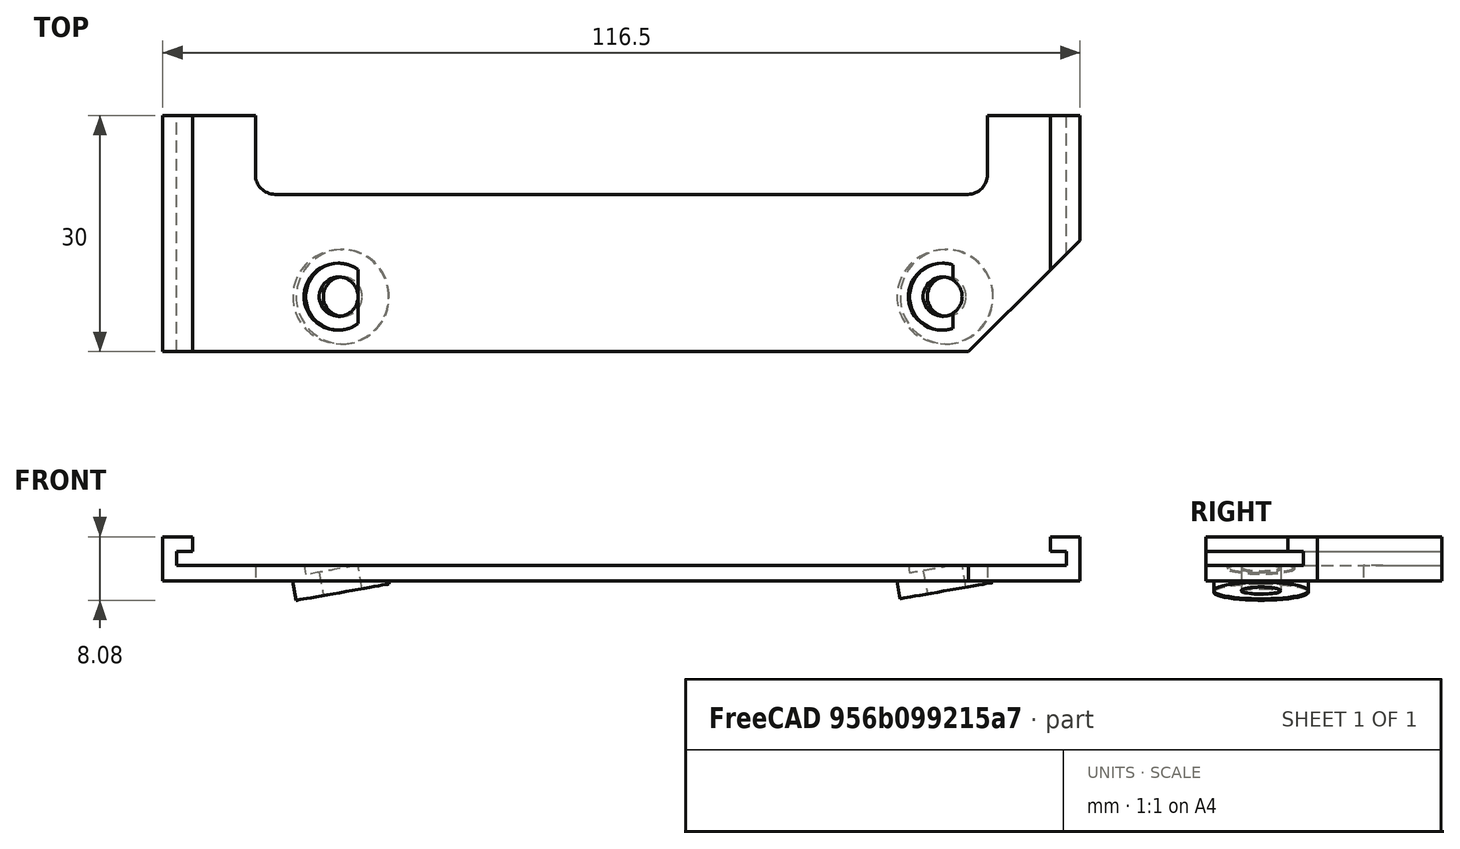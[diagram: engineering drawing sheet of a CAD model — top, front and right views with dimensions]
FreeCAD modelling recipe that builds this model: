
FCSTD DOCUMENT  (FreeCAD 0.21R33668 +7 (Git))
Label: DecentXL-Left-Bracket
License: All rights reserved
LicenseURL: http://en.wikipedia.org/wiki/All_rights_reserved
objects: Sketcher::SketchObject×9, PartDesign::Pocket×7, PartDesign::Line×2, PartDesign::Pad×2, Part::Box×1, PartDesign::FeatureBase×1, PartDesign::Body×1, Mesh::Feature×1
note: 32 computed .brp shape members not serialized (recipe doc carries the construction recipe); baked Part::Feature solids carry a one-line shape summary decoded from their .brp

FEATURE [Part::Box] Box  label="Cube"
  AttacherType = Attacher::AttachEngine3D
  Height = 5.6
  Length = 116.5
  Width = 30
FEATURE [PartDesign::FeatureBase] BaseFeature
  BaseFeature = -> Box
FEATURE [Sketcher::SketchObject] Sketch
  ExternalGeometry = -> [BaseFeature]
  FullyConstrained = true
  MapMode = 5
  Placement = pos=(0,0,0) rot=(1,0,0;1.5708rad)
  Support = -> [BaseFeature]
  sketch-geometry (10):
    g0: LineSegment StartX=3.75 StartY=5.6 StartZ=0 EndX=3.75 EndY=3.75 EndZ=0
    g1: LineSegment StartX=3.75 StartY=3.75 StartZ=0 EndX=1.75 EndY=3.75 EndZ=0
    g2: LineSegment StartX=1.75 StartY=3.75 StartZ=0 EndX=1.75 EndY=1.95 EndZ=0
    g3: LineSegment StartX=1.75 StartY=1.95 StartZ=0 EndX=114.75 EndY=1.95 EndZ=0
    g4: LineSegment StartX=114.75 StartY=1.95 StartZ=0 EndX=114.75 EndY=3.75 EndZ=0
    g5: LineSegment StartX=114.75 StartY=3.75 StartZ=0 EndX=112.75 EndY=3.75 EndZ=0
    g6: LineSegment StartX=112.75 StartY=3.75 StartZ=0 EndX=112.75 EndY=5.6 EndZ=0
    g7: LineSegment StartX=112.75 StartY=5.6 StartZ=0 EndX=3.75 EndY=5.6 EndZ=0
    g8: LineSegment StartX=0 StartY=5.6 StartZ=0 EndX=3.75 EndY=5.6 EndZ=0
    g9: LineSegment StartX=112.75 StartY=5.6 StartZ=0 EndX=116.5 EndY=5.6 EndZ=0
  constraints (28):
    c: PointOnObject(g0,g-3)
    c: Vertical(g0)
    c: Coincident(g0,g1)
    c: Horizontal(g1)
    c: Coincident(g1,g2)
    c: Vertical(g2)
    c: Coincident(g2,g3)
    c: Horizontal(g3)
    c: Coincident(g3,g4)
    c: Vertical(g4)
    c: Coincident(g4,g5)
    c: Horizontal(g5)
    c: Coincident(g5,g6)
    c: PointOnObject(g6,g-3)
    c: Vertical(g6)
    c: Coincident(g6,g7)
    c: Coincident(g7,g0)
    c: Equal(g2,g4)
    c: DistanceY(g4,g4) = 1.8
    c: DistanceX(g3,g3) = 113
    c: Equal(g1,g5)
    c: Coincident(g8,g-3)
    c: Coincident(g8,g0)
    c: Coincident(g9,g6)
    c: Coincident(g9,g-3)
    c: Equal(g8,g9)
    c: DistanceY(g6,g6) = 1.85
    c: DistanceX(g1,g1) = 2
FEATURE [PartDesign::Pocket] Pocket
  BaseFeature = -> BaseFeature
  Direction = (0,1,-2e-16)
  Length = 0
  Length2 = 5
  Profile = -> Sketch
  ReferenceAxis = -> Sketch [N_Axis]
  Type = 3
  UpToFace = -> BaseFeature [Face4]
FEATURE [Sketcher::SketchObject] Sketch001
  ExternalGeometry = -> [Pocket]
  FullyConstrained = true
  MapMode = 5
  Placement = pos=(0,0,0) rot=(1,0,0;3.14159rad)
  Support = -> [Pocket]
  sketch-geometry (3):
    g0: LineSegment StartX=102.358 StartY=-1.8e-15 StartZ=0 EndX=116.5 EndY=1e-16 EndZ=0
    g1: LineSegment StartX=116.5 StartY=1e-16 StartZ=0 EndX=116.5 EndY=-14.1421 EndZ=0
    g2: LineSegment StartX=116.5 StartY=-14.1421 StartZ=0 EndX=102.358 EndY=-1.8e-15 EndZ=0
  constraints (8):
    c: PointOnObject(g0,g-4)
    c: Coincident(g0,g-4)
    c: Coincident(g0,g1)
    c: PointOnObject(g1,g-3)
    c: Coincident(g1,g2)
    c: Coincident(g2,g0)
    c: Equal(g1,g0)
    c: Distance(g2) = 20
FEATURE [PartDesign::Pocket] Pocket001
  BaseFeature = -> Pocket
  Direction = (0,0,1)
  Length = 0
  Length2 = 5
  Profile = -> Sketch001
  ReferenceAxis = -> Sketch001 [N_Axis]
  Type = 3
  UpToFace = -> Pocket [Face7]
FEATURE [PartDesign::Line] DatumLine
  AttacherType = Attacher::AttachEngineLine
  AttachmentOffset = pos=(-20.5,0,0) rot=(0,0,1;0rad)
  Length = 20
  MapMode = 29
  Placement = pos=(22.25,4e-16,1.95) rot=(0,0.707107,0.707107;3.14159rad)
  ResizeMode = 0
  Support = -> [Pocket001]
FEATURE [Sketcher::SketchObject] Sketch002
  AttachmentOffset = pos=(0.607769,0,-7.3105) rot=(0,-1,0;0.174533rad)
  ExternalGeometry = -> [DatumLine]
  FullyConstrained = true
  MapMode = 5
  Placement = pos=(0.607769,-1.2e-15,-5.3605) rot=(0,-1,0;0.174533rad)
  Support = -> [Pocket001]
  expr: .AttachmentOffset.Base.x = 3.5 mm * sin(10)
  expr: .AttachmentOffset.Base.z = -sin(10) * DatumLine.Placement.Base.x - 3.5 mm * cos(10)
  sketch-geometry (1):
    g0: Circle CenterX=22.5829 CenterY=7 CenterZ=0 NormalX=0 NormalY=0 NormalZ=1 AngleXU=0 Radius=2.5
  constraints (3):
    c: PointOnObject(g0,g-3)
    c: Diameter(g0) = 5
    c: DistanceY(g-1,g0) = 7
FEATURE [Sketcher::SketchObject] Sketch003
  AttachmentOffset = pos=(0.607769,0,-7.3105) rot=(0,-1,0;0.174533rad)
  ExternalGeometry = -> [DatumLine]
  FullyConstrained = true
  MapMode = 5
  Placement = pos=(0.607769,-1.2e-15,-5.3605) rot=(0,-1,0;0.174533rad)
  Support = -> [Pocket001]
  expr: .AttachmentOffset.Base.x = 3.5 * sin(10)
  expr: .AttachmentOffset.Base.z = -sin(10) * DatumLine.Placement.Base.x - 3.5 mm * cos(10)
  sketch-geometry (1):
    g0: Circle CenterX=22.5829 CenterY=7 CenterZ=0 NormalX=0 NormalY=0 NormalZ=1 AngleXU=0 Radius=6
  constraints (3):
    c: Diameter(g0) = 12
    c: DistanceY(g-1,g0) = 7
    c: PointOnObject(g0,g-3)
FEATURE [PartDesign::Line] DatumLine001
  AttacherType = Attacher::AttachEngineLine
  AttachmentOffset = pos=(15.75,0,0) rot=(0,0,1;0rad)
  Length = 20
  MapMode = 29
  Placement = pos=(99,4e-16,1.95) rot=(0,0.707107,0.707107;3.14159rad)
  ResizeMode = 0
  Support = -> [Pocket]
FEATURE [Sketcher::SketchObject] Sketch005
  AttachmentOffset = pos=(0.607769,0,-20.638) rot=(0,-1,0;0.174533rad)
  ExternalGeometry = -> [DatumLine001]
  FullyConstrained = true
  MapMode = 5
  Placement = pos=(0.607769,-4.1e-15,-18.688) rot=(0,-1,0;0.174533rad)
  Support = -> [Pocket001]
  expr: .AttachmentOffset.Base.x = 3.5 mm * sin(10)
  expr: .AttachmentOffset.Base.z = -sin(10) * DatumLine001.Placement.Base.x - 3.5 mm * cos(10)
  sketch-geometry (1):
    g0: Circle CenterX=100.481 CenterY=7 CenterZ=0 NormalX=0 NormalY=0 NormalZ=1 AngleXU=0 Radius=6
  constraints (3):
    c: PointOnObject(g0,g-3)
    c: Diameter(g0) = 12
    c: DistanceY(g-1,g0) = 7
FEATURE [Sketcher::SketchObject] Sketch004
  AttachmentOffset = pos=(0.607769,0,-20.638) rot=(0,-1,0;0.174533rad)
  ExternalGeometry = -> [DatumLine001,Sketch005]
  FullyConstrained = true
  MapMode = 5
  Placement = pos=(0.607769,-4.1e-15,-18.688) rot=(0,-1,0;0.174533rad)
  Support = -> [Pocket001]
  expr: .AttachmentOffset.Base.x = 3.5 mm * sin(10)
  expr: .AttachmentOffset.Base.z = -sin(10) * DatumLine001.Placement.Base.x - 3.5 mm * cos(10)
  sketch-geometry (1):
    g0: Circle CenterX=100.481 CenterY=7 CenterZ=0 NormalX=0 NormalY=0 NormalZ=1 AngleXU=0 Radius=2.5
  constraints (2):
    c: Diameter(g0) = 5
    c: Coincident(g0,g-4)
FEATURE [PartDesign::Pad] Pad
  BaseFeature = -> Pocket001
  Direction = (-0.173648,2e-16,0.984808)
  Length = 1.4
  Length2 = 10
  Profile = -> Sketch003
  ReferenceAxis = -> Sketch003 [N_Axis]
  Reversed = true
  Type = 3
  UpToFace = -> Pocket001 [Face7]
FEATURE [PartDesign::Pad] Pad001
  BaseFeature = -> Pad
  Direction = (-0.173648,2e-16,0.984808)
  Length = 1.4
  Length2 = 10
  Profile = -> Sketch005
  ReferenceAxis = -> Sketch005 [N_Axis]
  Type = 3
  UpToFace = -> Pad [Face7]
FEATURE [PartDesign::Pocket] Pocket002
  BaseFeature = -> Pad001
  Direction = (0.173648,-2e-16,-0.984808)
  Length = 0
  Length2 = 5
  Midplane = true
  Profile = -> Sketch002
  ReferenceAxis = -> Sketch002 [N_Axis]
  Type = 3
  UpToFace = -> Pad001 [Face7]
FEATURE [Sketcher::SketchObject] Sketch006
  AttachmentOffset = pos=(0.0868241,0,-4.35608) rot=(0,-1,0;0.174533rad)
  ExternalGeometry = -> [Sketch003]
  FullyConstrained = true
  MapMode = 5
  Placement = pos=(0.0868241,-5e-16,-2.40608) rot=(0,-1,0;0.174533rad)
  Support = -> [Pocket001]
  expr: .AttachmentOffset.Base.x = 0.5 mm * sin(10)
  expr: .AttachmentOffset.Base.z = -sin(10) * DatumLine.Placement.Base.x - 0.5 mm * cos(10)
  sketch-geometry (1):
    g0: Circle CenterX=22.5829 CenterY=7 CenterZ=0 NormalX=0 NormalY=0 NormalZ=1 AngleXU=0 Radius=4.25
  constraints (2):
    c: Coincident(g0,g-3)
    c: Diameter(g0) = 8.5
FEATURE [PartDesign::Pocket] Pocket005
  BaseFeature = -> Pocket002
  Direction = (0.173648,-2e-16,-0.984808)
  Length = 5
  Length2 = 5
  Profile = -> Sketch006
  ReferenceAxis = -> Sketch006 [N_Axis]
  Reversed = true
  Type = 0
FEATURE [PartDesign::Pocket] Pocket004
  BaseFeature = -> Pocket005
  Direction = (0.173648,-2e-16,-0.984808)
  Length = 0
  Length2 = 5
  Midplane = true
  Profile = -> Sketch004
  ReferenceAxis = -> Sketch004 [N_Axis]
  Type = 3
  UpToFace = -> Pocket005 [Face7]
FEATURE [Sketcher::SketchObject] Sketch007
  AttachmentOffset = pos=(0.0868241,0,-17.6836) rot=(0,-1,0;0.174533rad)
  ExternalGeometry = -> [Sketch004]
  FullyConstrained = true
  MapMode = 5
  Placement = pos=(0.0868241,-3.5e-15,-15.7336) rot=(0,-1,0;0.174533rad)
  Support = -> [Pocket001]
  expr: .AttachmentOffset.Base.x = 0.5 * sin(10)
  expr: .AttachmentOffset.Base.z = -sin(10) * DatumLine001.Placement.Base.x - 0.5 mm * cos(10)
  sketch-geometry (1):
    g0: Circle CenterX=100.481 CenterY=7 CenterZ=0 NormalX=0 NormalY=0 NormalZ=1 AngleXU=0 Radius=4.25
  constraints (2):
    c: Coincident(g0,g-3)
    c: Diameter(g0) = 8.5
FEATURE [PartDesign::Pocket] Pocket006
  BaseFeature = -> Pocket004
  Direction = (0.173648,-2e-16,-0.984808)
  Length = 5
  Length2 = 5
  Profile = -> Sketch007
  ReferenceAxis = -> Sketch007 [N_Axis]
  Reversed = true
  Type = 0
FEATURE [Sketcher::SketchObject] Sketch008
  ExternalGeometry = -> [Pocket006]
  FullyConstrained = true
  MapMode = 5
  Placement = pos=(0,4e-16,1.95) rot=(0,0,1;0rad)
  Support = -> [Pocket006]
  sketch-geometry (10):
    g0: ArcOfCircle CenterX=14.25 CenterY=32.5 CenterZ=0 NormalX=0 NormalY=0 NormalZ=1 AngleXU=0 Radius=2.5 StartAngle=1.5708 EndAngle=3.14159
    g1: LineSegment StartX=14.25 StartY=35 StartZ=0 EndX=102.25 EndY=35 EndZ=0
    g2: ArcOfCircle CenterX=102.25 CenterY=32.5 CenterZ=0 NormalX=0 NormalY=0 NormalZ=1 AngleXU=0 Radius=2.5 StartAngle=6e-16 EndAngle=1.5708
    g3: LineSegment StartX=104.75 StartY=32.5 StartZ=0 EndX=104.75 EndY=22.5 EndZ=0
    g4: ArcOfCircle CenterX=102.25 CenterY=22.5 CenterZ=0 NormalX=0 NormalY=0 NormalZ=1 AngleXU=0 Radius=2.5 StartAngle=4.71239 EndAngle=6.28319
    g5: LineSegment StartX=102.25 StartY=20 StartZ=0 EndX=14.25 EndY=20 EndZ=0
    g6: ArcOfCircle CenterX=14.25 CenterY=22.5 CenterZ=0 NormalX=0 NormalY=0 NormalZ=1 AngleXU=0 Radius=2.5 StartAngle=3.14159 EndAngle=4.71239
    g7: LineSegment StartX=11.75 StartY=22.5 StartZ=0 EndX=11.75 EndY=32.5 EndZ=0
    g8: GeomPoint X=11.75 Y=35 Z=0
    g9: GeomPoint X=104.75 Y=20 Z=0
  constraints (24):
    c: Tangent(g0,g1) = 1.5708
    c: Tangent(g1,g2) = 1.5708
    c: Tangent(g2,g3) = 1.5708
    c: Tangent(g3,g4) = 1.5708
    c: Tangent(g4,g5) = 1.5708
    c: Tangent(g5,g6) = 1.5708
    c: Tangent(g6,g7) = 1.5708
    c: Tangent(g7,g0) = 1.5708
    c: Horizontal(g1)
    c: Horizontal(g5)
    c: Vertical(g3)
    c: Vertical(g7)
    c: Equal(g0,g2)
    c: Equal(g2,g4)
    c: Equal(g4,g6)
    c: PointOnObject(g8,g1)
    c: PointOnObject(g8,g7)
    c: PointOnObject(g9,g3)
    c: PointOnObject(g9,g5)
    c: Diameter(g0) = 5
    c: DistanceY(g5,g-3) = 10
    c: DistanceX(g-3,g6) = 10
    c: DistanceX(g3,g-3) = 10
    c: DistanceY(g4,g1) = 15
FEATURE [PartDesign::Pocket] Pocket007
  BaseFeature = -> Pocket006
  Direction = (0,-2e-16,-1)
  Length = 5
  Length2 = 5
  Profile = -> Sketch008
  ReferenceAxis = -> Sketch008 [N_Axis]
  Type = 1
FEATURE [PartDesign::Body] Body
  BaseFeature = -> Box
  Group = -> [BaseFeature,Sketch,Pocket,Sketch001,Pocket001,DatumLine,Sketch002,Pad,Pad001,Pocket002,Sketch003,DatumLine001,Sketch004,Sketch006,Pocket005,Pocket004,Sketch005,Sketch007,Pocket006,Sketch008,Pocket007]
  Origin = -> Origin
  Tip = -> Pocket007
FEATURE [Mesh::Feature] Mesh  label="Pocket007 (Meshed)"
